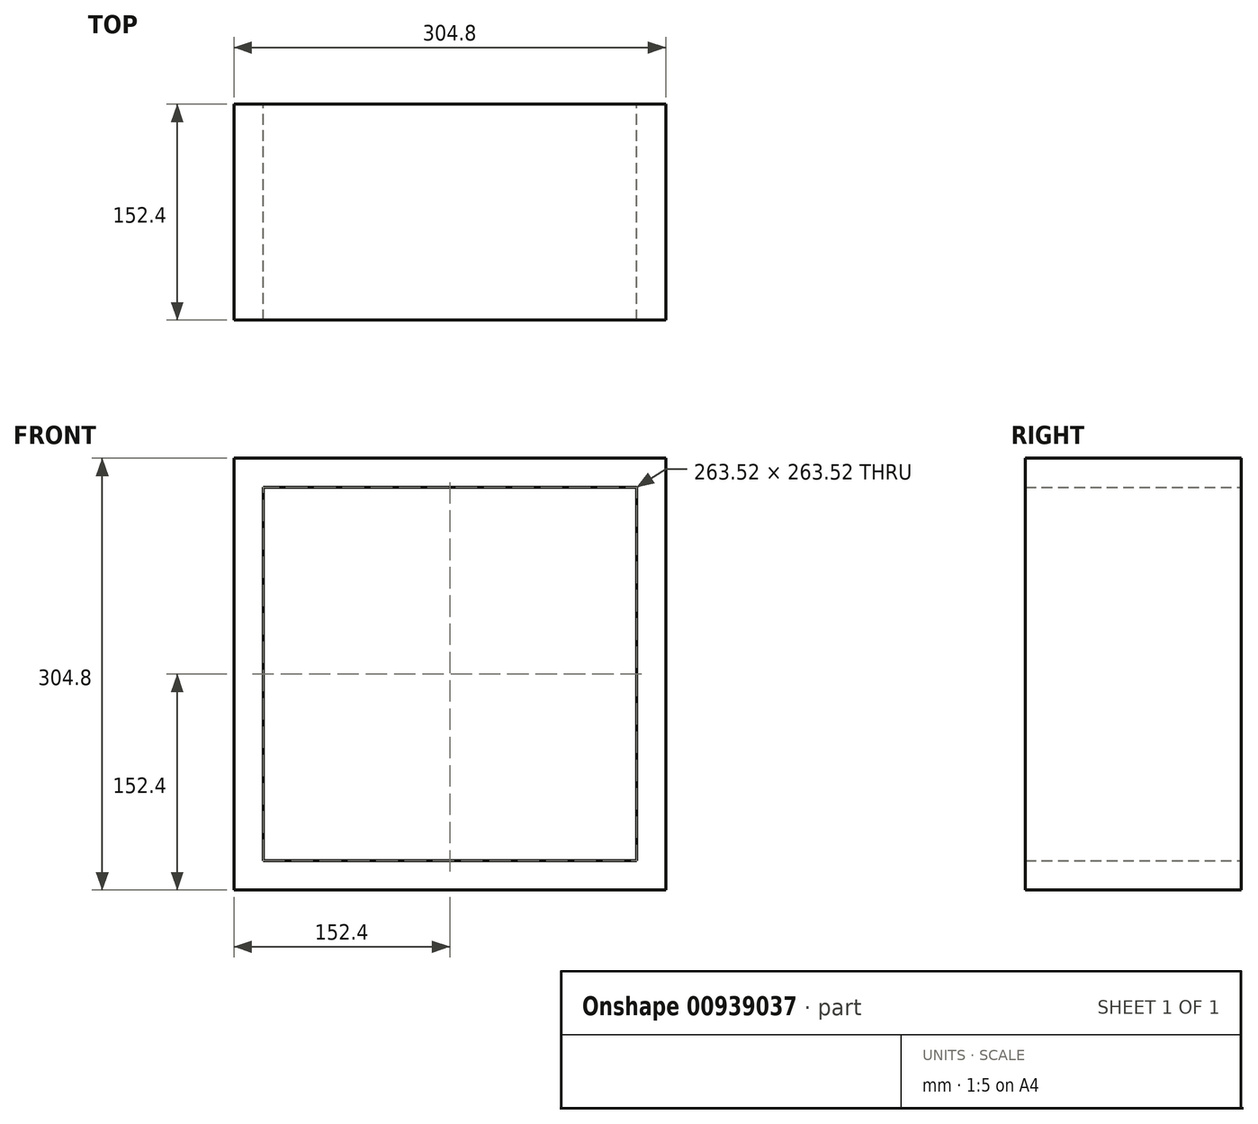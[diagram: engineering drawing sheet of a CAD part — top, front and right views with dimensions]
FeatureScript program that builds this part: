
annotation { "Feature Type Name" : "Feature", "Feature Type Description" : "" }
export const myFeature = defineFeature(function(context is Context, id is Id, definition is map)
    precondition{}
    {
        {
            var Q0;
            Q0=qCreatedBy(makeId("Front.planeOp"),FACE);
            var sketch = newSketch(context, id + "F0", { "sketchPlane" : qUnion([Q0])});
            skLineSegment(sketch, "E0.bottom", {"start": v(-131.76, 131.76) * mm, "end": v(131.76, 131.76) * mm});
            skLineSegment(sketch, "E0.top", {"start": v(-131.76, -131.76) * mm, "end": v(131.76, -131.76) * mm});
            skLineSegment(sketch, "E0.left", {"start": v(-131.76, 131.76) * mm, "end": v(-131.76, -131.76) * mm});
            skLineSegment(sketch, "E0.right", {"start": v(131.76, 131.76) * mm, "end": v(131.76, -131.76) * mm});
            skPoint(sketch, "E0.middle", {"position": v(0, 0) * mm});
            skLineSegment(sketch, "E1.bottom", {"start": v(-152.4, 152.4) * mm, "end": v(152.4, 152.4) * mm});
            skLineSegment(sketch, "E1.top", {"start": v(-152.4, -152.4) * mm, "end": v(152.4, -152.4) * mm});
            skLineSegment(sketch, "E1.left", {"start": v(-152.4, 152.4) * mm, "end": v(-152.4, -152.4) * mm});
            skLineSegment(sketch, "E1.right", {"start": v(152.4, 152.4) * mm, "end": v(152.4, -152.4) * mm});
            skSolve(sketch);
        }
        {
            var Q0;
            Q0=makeQuery(id+"F0.imprint","IMPRINT",FACE,{"disambiguationData":[TD([[makeQuery(id+"F0.imprint","IMPRINT",EDGE,{"derivedFrom":sQuery(id+"F0.wireOp",EDGE,"E0.bottom")}),1.0]])]});
            extrude(context, id + "F1", {"entities" : qUnion([Q0]), "depth" : 152.4 * mm, "offsetDistance" : 25.4 * mm});
        }
    });
